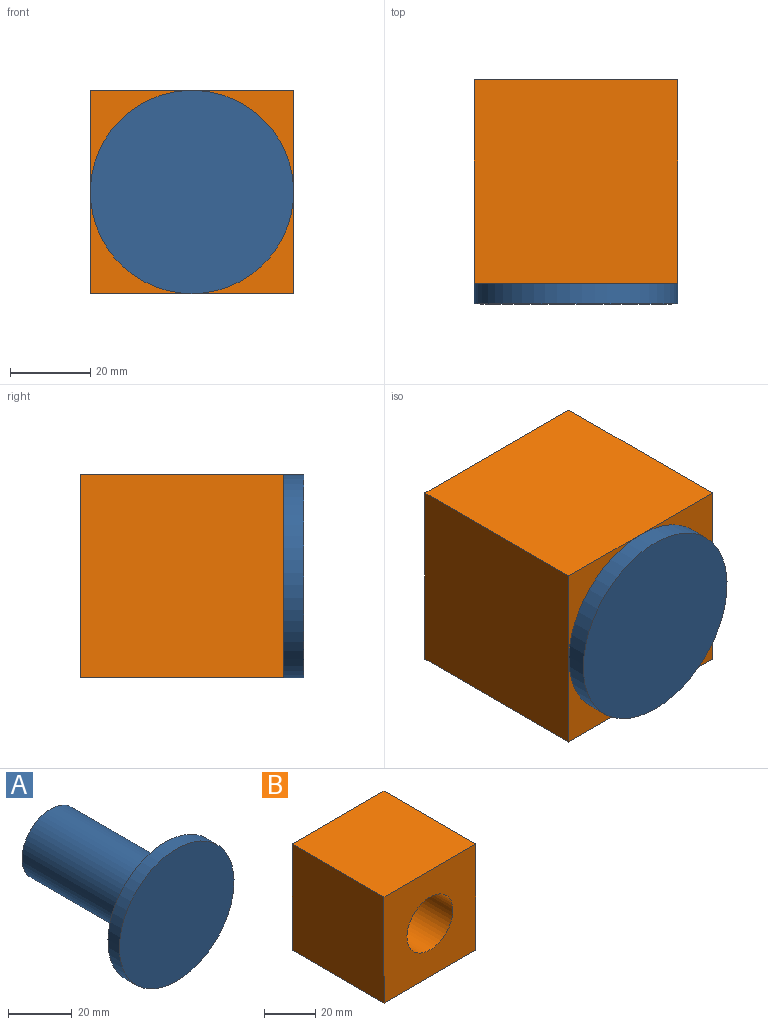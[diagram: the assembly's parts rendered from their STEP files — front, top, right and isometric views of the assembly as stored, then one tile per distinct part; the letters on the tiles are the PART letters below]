
ASSEMBLY  parts=2 mates=1
PART A: 5 faces, bbox 50.8x55.9x50.8 mm
  f0: cylinder r=12.7mm len=50.8mm, axis (0,1,0), area 4053.7mm2, adj f1,f4
  f1: plane 25.4x25.4mm, normal (0,1,0), area 506.7mm2, adj f0
  f2: cylinder r=25.4mm len=50.8mm, axis (0,1,0), area 810.7mm2, adj f3,f4
  f3: plane 50.8x50.8mm, normal (0,-1,0), area 2026.8mm2, adj f2
  f4: plane 50.8x50.8mm, normal (0,1,0), area 1520.1mm2, adj f0,f2
PART B: 7 faces, bbox 50.8x50.8x50.8 mm
  f0: plane 50.8x50.8mm, normal (-1,0,0), area 2580.6mm2, adj f1,f3,f4,f5
  f1: plane 50.8x50.8mm, normal (0,0,-1), area 2580.6mm2, adj f0,f2,f4,f5
  f2: plane 50.8x50.8mm, normal (1,0,0), area 2580.6mm2, adj f1,f3,f4,f5
  f3: plane 50.8x50.8mm, normal (0,0,1), area 2580.6mm2, adj f0,f2,f4,f5
  f4: plane 50.8x50.8mm, normal (0,-1,0), area 2073.9mm2, adj f0,f1,f2,f3,f6
  f5: plane 50.8x50.8mm, normal (0,1,0), area 2073.9mm2, adj f0,f1,f2,f3,f6
  f6: cylinder r=12.7mm len=50.8mm, axis (0,-1,0), area 4053.7mm2, adj f4,f5
PLACE A t=(23.26,49.58,30.52)mm
PLACE B t=(-2.14,49.65,5.12)mm
MATE cylindrical A.f0 <-> B.f6  axis (0,1,0) through (23.26,24.18,30.52)mm
